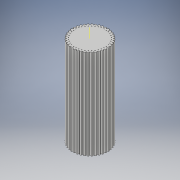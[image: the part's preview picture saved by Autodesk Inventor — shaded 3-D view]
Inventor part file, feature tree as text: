
AUTODESK INVENTOR PART (.ipt)
format: ipt  version: 2019.3 (Build 233278000, 278)  size: 694,784 bytes
history: native  units: mm
features: extrude x1
ambient origin geometry x8: Origin, YZ Plane, XZ Plane, XY Plane, X Axis, Y Axis, Z Axis, Center Point
bodies: Body1 (feature_tree)
feature tree (1):
  extrude  "Extrusion2"  Depth=5.047545mm
